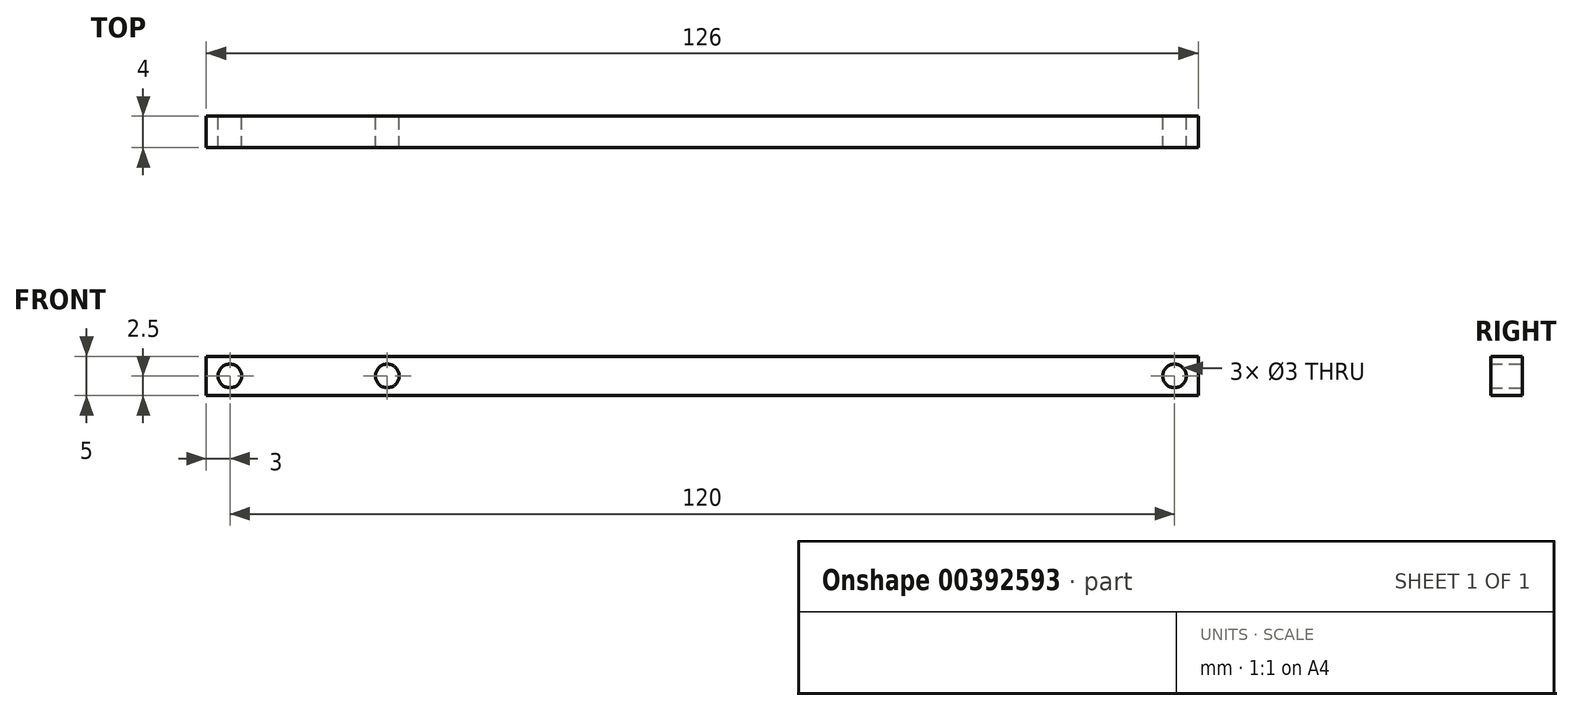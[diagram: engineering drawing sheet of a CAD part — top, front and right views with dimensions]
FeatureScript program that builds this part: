
annotation { "Feature Type Name" : "Feature", "Feature Type Description" : "" }
export const myFeature = defineFeature(function(context is Context, id is Id, definition is map)
    precondition{}
    {
        {
            var Q0;
            Q0=qCreatedBy(makeId("Front.planeOp"),FACE);
            var sketch = newSketch(context, id + "F0", { "sketchPlane" : qUnion([Q0])});
            skLineSegment(sketch, "E0.bottom", {"start": v(-63, 0) * mm, "end": v(63, 0) * mm});
            skLineSegment(sketch, "E0.top", {"start": v(-63, 5) * mm, "end": v(63, 5) * mm});
            skLineSegment(sketch, "E0.left", {"start": v(-63, 0) * mm, "end": v(-63, 5) * mm});
            skLineSegment(sketch, "E0.right", {"start": v(63, 0) * mm, "end": v(63, 5) * mm});
            skCircle(sketch, "E1", {"center": v(60, 2.5) * mm, "radius": 1.5 * mm});
            skCircle(sketch, "E2.1.0.0", {"center": v(-60, 2.5) * mm, "radius": 1.5 * mm});
            skLineSegment(sketch, "E2.direction1", {"start": v(60, 2.5) * mm, "end": v(-60, 2.5) * mm, "construction": true});
            skCircle(sketch, "E3", {"center": v(-40, 2.5) * mm, "radius": 1.5 * mm});
            skSolve(sketch);
        }
        {
            var Q0;
            Q0=makeQuery(id+"F0.imprint","IMPRINT",FACE,{"disambiguationData":[TD([[makeQuery(id+"F0.imprint","IMPRINT",EDGE,{"derivedFrom":sQuery(id+"F0.wireOp",EDGE,"E0.bottom")}),1.0]])]});
            var Q1;
            Q1=sQuery(id+"F0.wireOp",EDGE,"E0.top");
            extrude(context, id + "F1", {"entities" : qUnion([Q0]), "surfaceEntities" : qUnion([Q1]), "depth" : 4 * mm});
        }
    });
